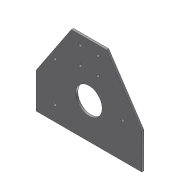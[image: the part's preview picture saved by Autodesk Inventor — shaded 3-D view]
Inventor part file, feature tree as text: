
AUTODESK INVENTOR PART (.ipt)
format: ipt  version: 2012 (Build 160160000, 160)  size: 105,984 bytes
history: native  units: in
note: dims shown in document units (in); Inventor stores cm internally (conversion verified against a paired STEP export)
features: extrude x4, sketch x4
ambient origin geometry x8: Origin, YZ Plane, XZ Plane, XY Plane, X Axis, Y Axis, Z Axis, Center Point
bodies: Solid1 (feature_tree)
feature tree (8):
  extrude  "Extrusion1"  Depth=2.0in
  extrude  "Extrusion2"  Depth=0.1875in
  extrude  "Extrusion3"  Depth=1.0in
  extrude  "Extrusion4"  Depth=1.0in
  sketch  "Sketch1"  dims[d0=2.0in d3=2.0in]
  sketch  "Sketch2"  dims[d4=0.125in d5=0.0in d6=0.1875in]
  sketch  "Sketch3"  dims[d7=0.5in d8=1.0in]
  sketch  "Sketch4"  dims[d9=0.5in d10=1.0in d11=1.0in d12=0.0in d13=1.0in d14=1.5in d15=1.0in d16=0.0in d17=5.0in d18=2.0in d20=0.1875in d23=2.25in d24=1.0in d25=0.0in d26=6.0in]
